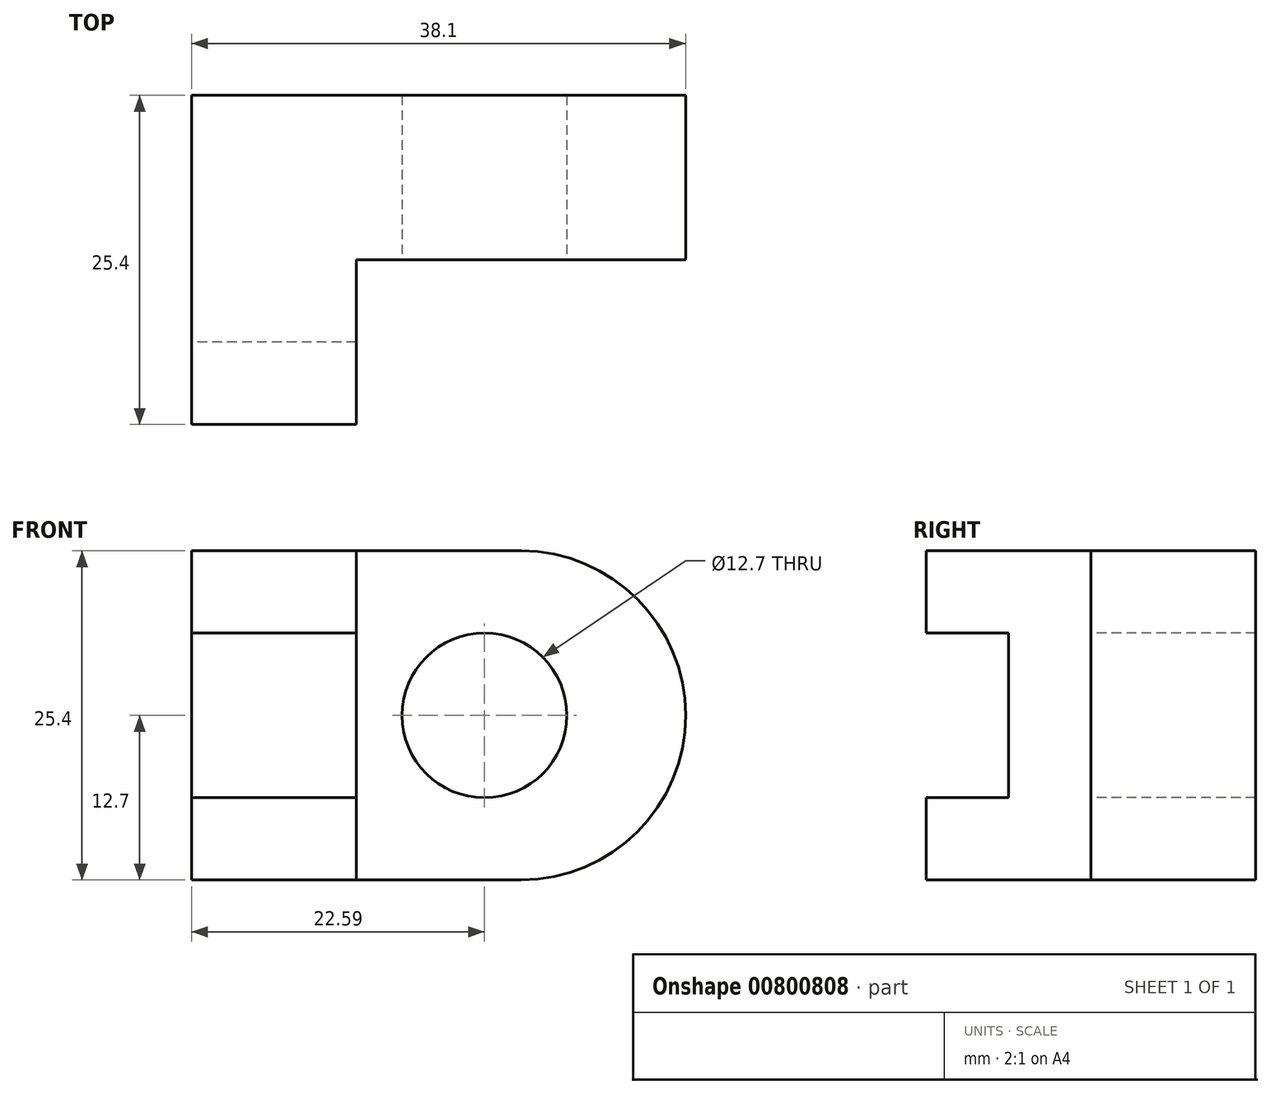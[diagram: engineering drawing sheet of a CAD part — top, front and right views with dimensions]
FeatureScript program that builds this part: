
annotation { "Feature Type Name" : "Feature", "Feature Type Description" : "" }
export const myFeature = defineFeature(function(context is Context, id is Id, definition is map)
    precondition{}
    {
        {
            var Q0;
            Q0=qCreatedBy(makeId("Right.planeOp"),FACE);
            var sketch = newSketch(context, id + "F0", { "sketchPlane" : qUnion([Q0])});
            skLineSegment(sketch, "E0", {"start": v(0, 0) * mm, "end": v(25.4, 0) * mm});
            skLineSegment(sketch, "E1", {"start": v(25.4, 0) * mm, "end": v(25.4, 25.4) * mm});
            skLineSegment(sketch, "E2", {"start": v(25.4, 25.4) * mm, "end": v(0, 25.4) * mm});
            skLineSegment(sketch, "E3", {"start": v(0, 25.4) * mm, "end": v(0, 19.05) * mm});
            skLineSegment(sketch, "E4", {"start": v(0, 19.05) * mm, "end": v(6.35, 19.05) * mm});
            skLineSegment(sketch, "E5", {"start": v(6.35, 19.05) * mm, "end": v(6.35, 6.35) * mm});
            skLineSegment(sketch, "E6", {"start": v(6.35, 6.35) * mm, "end": v(0, 6.35) * mm});
            skLineSegment(sketch, "E7", {"start": v(0, 6.35) * mm, "end": v(0, 0) * mm});
            skSolve(sketch);
        }
        {
            var Q0;
            Q0=makeQuery(id+"F0.imprint","IMPRINT",FACE,{"disambiguationData":[TD([[makeQuery(id+"F0.imprint","IMPRINT",EDGE,{"derivedFrom":sQuery(id+"F0.wireOp",EDGE,"E0")}),1.0]])]});
            extrude(context, id + "F1", {"entities" : qUnion([Q0]), "depth" : 101.6 * mm, "offsetDistance" : 25.4 * mm});
        }
        {
            var Q0;
            Q0=makeQuery(id+"F1.opExtrude","SWEPT_FACE",FACE,{"disambiguationData":[OSD([sQuery(id+"F0.wireOp",EDGE,"E2")])]});
            var sketch = newSketch(context, id + "F2", { "sketchPlane" : qUnion([Q0])});
            skLineSegment(sketch, "E8", {"start": v(0, 0) * mm, "end": v(12.7, 0) * mm});
            skLineSegment(sketch, "E9", {"start": v(12.7, 0) * mm, "end": v(12.7, 12.7) * mm});
            skLineSegment(sketch, "E10", {"start": v(12.7, 12.7) * mm, "end": v(101.6, 12.7) * mm});
            skSolve(sketch);
        }
        {
            var Q0;
            {var subQ0=sQuery(id+"F2.wireOp",EDGE,"E9");Q0=makeQuery(id+"F2.imprint","IMPRINT",FACE,{"disambiguationData":[TD([[makeQuery(id+"F2.imprint","IMPRINT",EDGE,{"derivedFrom":subQ0}),-1.0]])]});}
            extrude(context, id + "F3", {"entities" : qUnion([Q0]), "operationType" : NewBodyOperationType.REMOVE, "oppositeDirection" : true, "depth" : 25.4 * mm, "offsetDistance" : 25.4 * mm});
        }
        {
            var Q0;
            Q0=makeQuery(id+"F3.boolean.opBoolean","COPY",FACE,{"derivedFrom":makeQuery(id+"F3.opExtrude","SWEPT_FACE",FACE,{"disambiguationData":[OSD([sQuery(id+"F2.wireOp",EDGE,"E10")])]})});
            var sketch = newSketch(context, id + "F4", { "sketchPlane" : qUnion([Q0])});
            skLineSegment(sketch, "E11", {"start": v(12.7, 0) * mm, "end": v(25.4, 0) * mm, "construction": true});
            skLineSegment(sketch, "E12", {"start": v(12.7, 25.4) * mm, "end": v(25.4, 25.4) * mm, "construction": true});
            skArc(sketch, "E13", {"start": v(25.4, 0) * mm, "mid": v(38.1, 12.7) * mm, "end": v(25.4, 25.4) * mm});
            skSolve(sketch);
        }
        {
            var Q0;
            {var subQ0=sQuery(id+"F4.wireOp",EDGE,"E13");Q0=makeQuery(id+"F4.imprint","IMPRINT",FACE,{"disambiguationData":[TD([[makeQuery(id+"F4.imprint","IMPRINT",EDGE,{"derivedFrom":subQ0}),-1.0]])]});}
            extrude(context, id + "F5", {"entities" : qUnion([Q0]), "operationType" : NewBodyOperationType.REMOVE, "oppositeDirection" : true, "depth" : 25.4 * mm, "offsetDistance" : 25.4 * mm});
        }
        {
            var Q0;
            Q0=makeQuery(id+"F3.boolean.opBoolean","COPY",FACE,{"derivedFrom":makeQuery(id+"F3.opExtrude","SWEPT_FACE",FACE,{"disambiguationData":[OSD([sQuery(id+"F2.wireOp",EDGE,"E10")])]})});
            var sketch = newSketch(context, id + "F6", { "sketchPlane" : qUnion([Q0])});
            skLineSegment(sketch, "E14", {"start": v(12.7, 0) * mm, "end": v(12.7, 12.7) * mm, "construction": true});
            skLineSegment(sketch, "E15", {"start": v(12.7, 12.7) * mm, "end": v(22.6, 12.7) * mm, "construction": true});
            skCircle(sketch, "E16", {"center": v(22.6, 12.7) * mm, "radius": 6.35 * mm});
            skSolve(sketch);
        }
        {
            var Q0;
            Q0=makeQuery(id+"F6.imprint","IMPRINT",FACE,{"disambiguationData":[TD([[makeQuery(id+"F6.imprint","IMPRINT",EDGE,{"derivedFrom":sQuery(id+"F6.wireOp",EDGE,"E16")}),1.0]])]});
            extrude(context, id + "F7", {"entities" : qUnion([Q0]), "operationType" : NewBodyOperationType.REMOVE, "oppositeDirection" : true, "depth" : 25.4 * mm, "offsetDistance" : 25.4 * mm});
        }
    });
